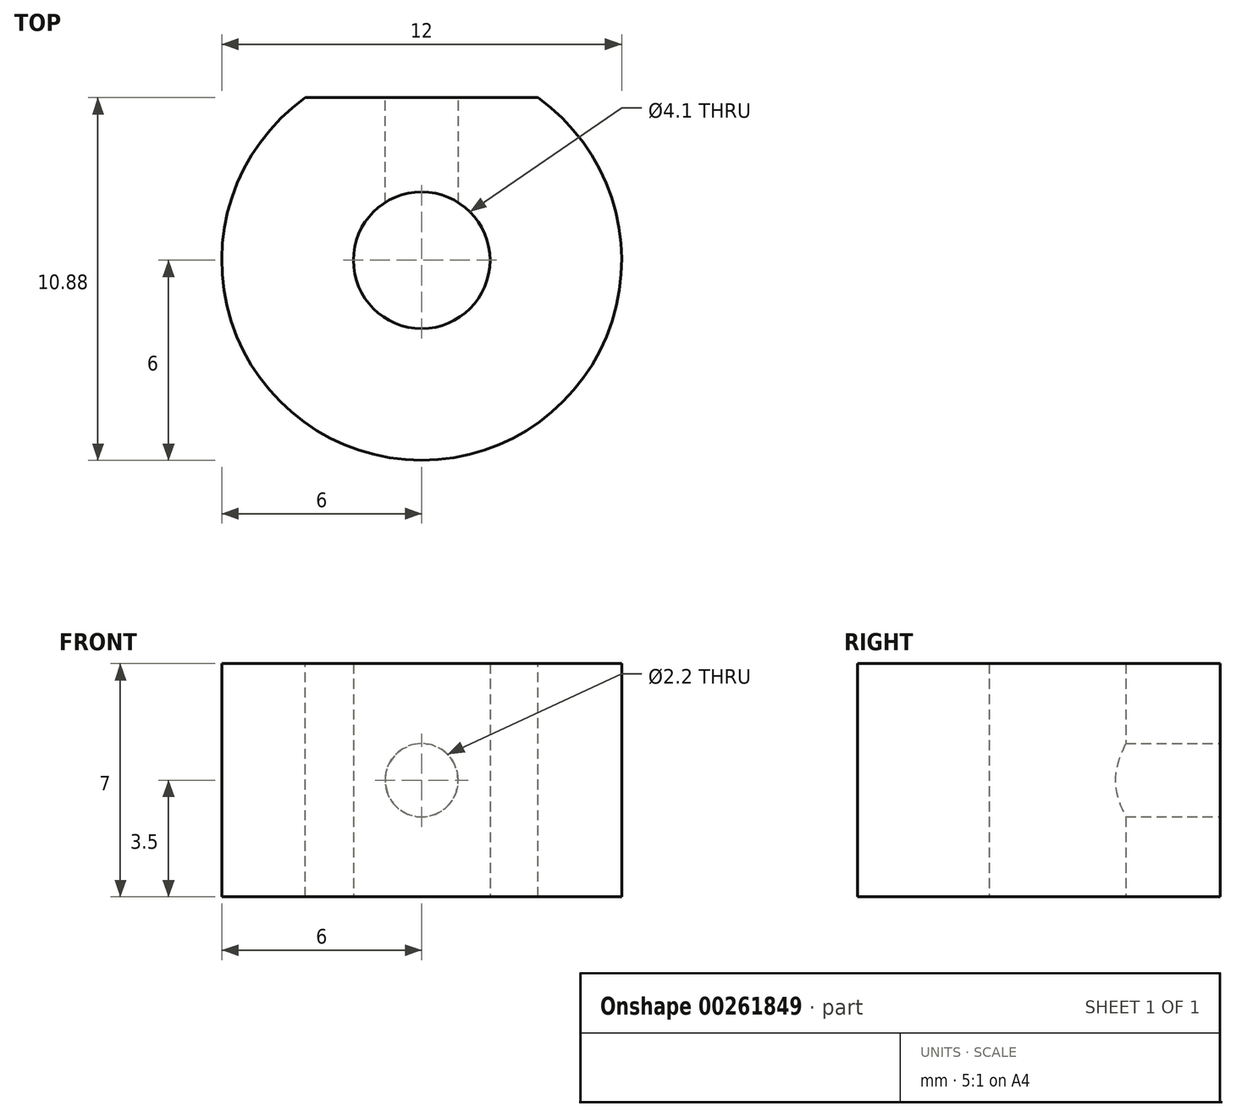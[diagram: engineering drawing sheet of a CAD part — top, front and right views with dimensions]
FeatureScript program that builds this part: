
annotation { "Feature Type Name" : "Feature", "Feature Type Description" : "" }
export const myFeature = defineFeature(function(context is Context, id is Id, definition is map)
    precondition{}
    {
        {
            var Q0;
            Q0=qCreatedBy(makeId("Top.planeOp"),FACE);
            var sketch = newSketch(context, id + "F0", { "sketchPlane" : qUnion([Q0])});
            skCircle(sketch, "E0", {"center": v(0, 0) * mm, "radius": 6 * mm});
            skCircle(sketch, "E1", {"center": v(0, 0) * mm, "radius": 2.05 * mm});
            skSolve(sketch);
        }
        {
            var Q0;
            Q0=makeQuery(id+"F0.imprint","IMPRINT",FACE,{"disambiguationData":[TD([[makeQuery(id+"F0.imprint","IMPRINT",EDGE,{"derivedFrom":sQuery(id+"F0.wireOp",EDGE,"E0")}),1.0]])]});
            extrude(context, id + "F1", {"entities" : qUnion([Q0]), "depth" : 7 * mm});
        }
        {
            var Q0;
            Q0=makeQuery(id+"F1.opExtrude","CAP_FACE",FACE,{"disambiguationData":[OSD([sQuery(id+"F0.wireOp",EDGE,"E0"),sQuery(id+"F0.wireOp",EDGE,"E1")])],"isStart":false});
            var sketch = newSketch(context, id + "F2", { "sketchPlane" : qUnion([Q0])});
            skLineSegment(sketch, "E2", {"start": v(-3.5, 4.88) * mm, "end": v(3.5, 4.88) * mm});
            skSolve(sketch);
        }
        {
            var Q0;
            {var subQ0=sQuery(id+"F2.wireOp",EDGE,"E2");Q0=makeQuery(id+"F2.imprint","IMPRINT",FACE,{"disambiguationData":[TD([[makeQuery(id+"F2.imprint","IMPRINT",EDGE,{"derivedFrom":subQ0}),1.0]])]});}
            extrude(context, id + "F3", {"entities" : qUnion([Q0]), "operationType" : NewBodyOperationType.REMOVE, "endBound" : BoundingType.THROUGH_ALL, "oppositeDirection" : true, "depth" : 25 * mm});
        }
        {
            var Q0;
            Q0=makeQuery(id+"F3.boolean.opBoolean","COPY",FACE,{"derivedFrom":makeQuery(id+"F3.opExtrude","SWEPT_FACE",FACE,{"disambiguationData":[OSD([sQuery(id+"F2.wireOp",EDGE,"E2")])]})});
            var sketch = newSketch(context, id + "F4", { "sketchPlane" : qUnion([Q0])});
            skLineSegment(sketch, "E3", {"start": v(3.5, 0) * mm, "end": v(-3.5, 7) * mm, "construction": true});
            skLineSegment(sketch, "E4", {"start": v(-3.5, 7) * mm, "end": v(3.5, 7) * mm, "construction": true});
            skLineSegment(sketch, "E5", {"start": v(3.5, 7) * mm, "end": v(-3.5, 0) * mm, "construction": true});
            skPoint(sketch, "E6", {"position": v(0, 3.5) * mm});
            skCircle(sketch, "E7", {"center": v(0, 3.5) * mm, "radius": 1.1 * mm});
            skSolve(sketch);
        }
        {
            var Q0;
            Q0=makeQuery(id+"F4.imprint","IMPRINT",FACE,{"disambiguationData":[TD([[makeQuery(id+"F4.imprint","IMPRINT",EDGE,{"derivedFrom":sQuery(id+"F4.wireOp",EDGE,"E7")}),1.0]])]});
            extrude(context, id + "F5", {"entities" : qUnion([Q0]), "operationType" : NewBodyOperationType.REMOVE, "oppositeDirection" : true, "depth" : 4 * mm});
        }
    });
